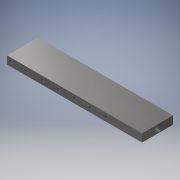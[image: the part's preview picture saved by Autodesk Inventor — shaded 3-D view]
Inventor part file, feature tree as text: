
AUTODESK INVENTOR PART (.ipt)
format: ipt  version: 2018 (Build 220112000, 112)  size: 279,040 bytes
history: native  units: mm
features: hole x8, extrude x1, pattern_linear x1, thread x1
ambient origin geometry x8: Origin, YZ Plane, XZ Plane, XY Plane, X Axis, Y Axis, Z Axis, Center Point
bodies: Volumenkörper1 (feature_tree)
feature tree (11):
  extrude  "Extrusion1"  Depth=39.0mm
  hole  "Bohrung7"  [1 undecoded]
  hole  "Bohrung8"  [1 undecoded]
  hole  "Bohrung9"  [1 undecoded]
  hole  "Bohrung10"  [1 undecoded]
  pattern_linear  "Rechteckige Anordnung3"  Spacing1=18.8mm  [1 undecoded]
  hole  "Bohrung25"  [1 undecoded]
  hole  "Bohrung26"  [1 undecoded]
  hole  "Bohrung27"  [1 undecoded]
  hole  "Bohrung28"  [1 undecoded]
  thread  "Thread1"  [1 undecoded]
note: 10 required parameter values undecoded (feature->parameter linkage not recoverable at this tier; creation-order binding heuristic only, values carry confidence <= 0.55)
